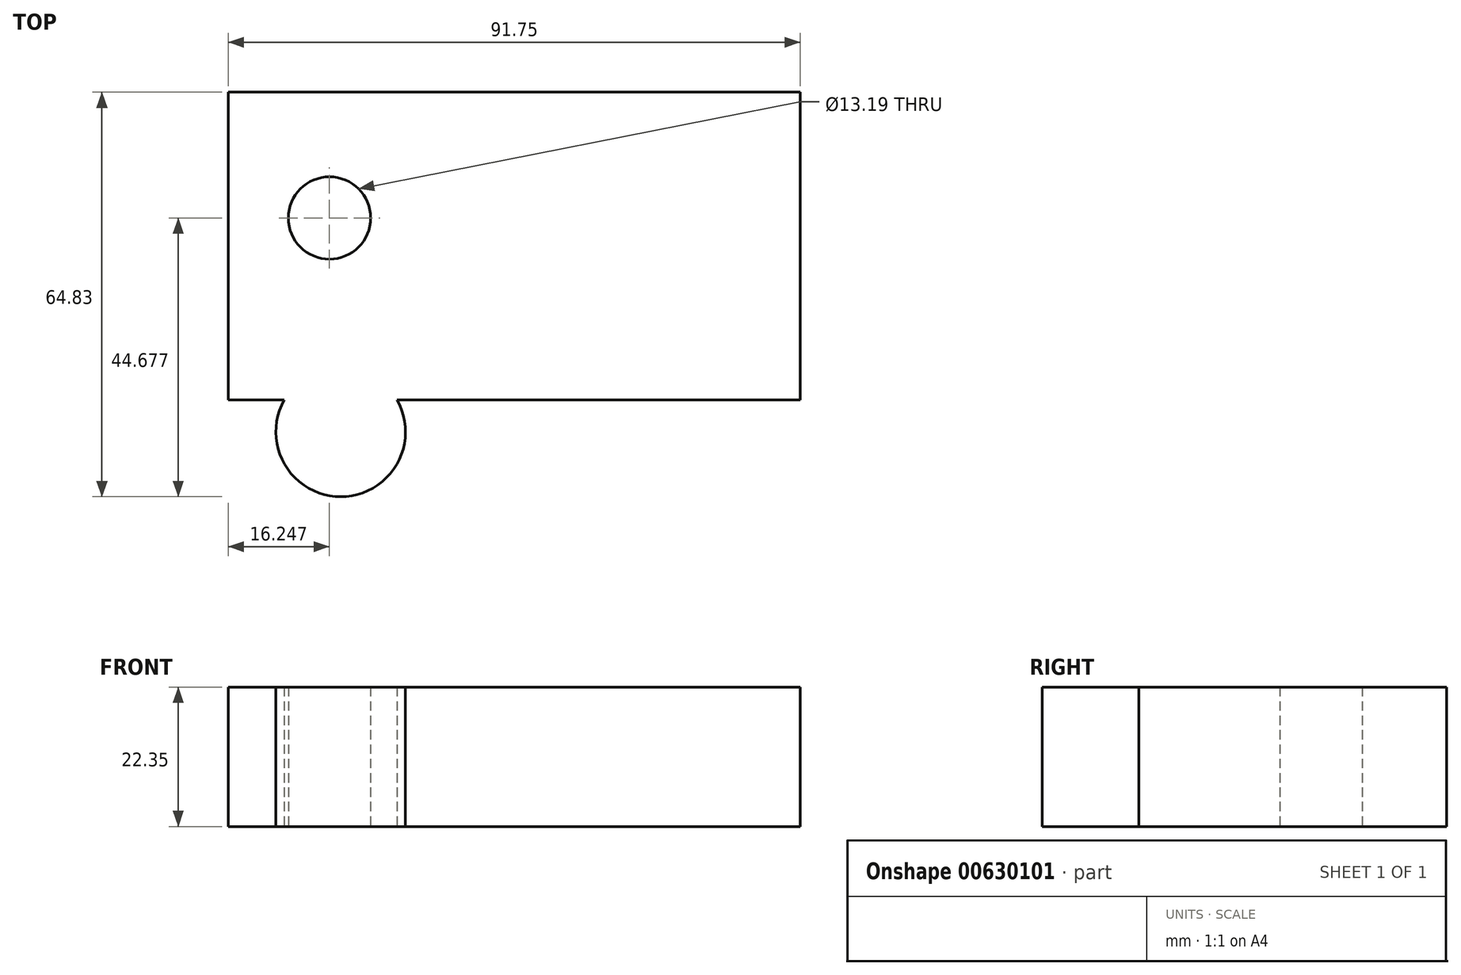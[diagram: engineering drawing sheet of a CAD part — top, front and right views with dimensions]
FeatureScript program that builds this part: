
annotation { "Feature Type Name" : "Feature", "Feature Type Description" : "" }
export const myFeature = defineFeature(function(context is Context, id is Id, definition is map)
    precondition{}
    {
        {
            var Q0;
            Q0=qCreatedBy(makeId("Top.planeOp"),FACE);
            var sketch = newSketch(context, id + "F0", { "sketchPlane" : qUnion([Q0])});
            skLineSegment(sketch, "E0.bottom", {"start": v(-44.07, 30.53) * mm, "end": v(47.68, 30.53) * mm});
            skLineSegment(sketch, "E0.top", {"start": v(-44.07, -18.8) * mm, "end": v(47.68, -18.8) * mm});
            skLineSegment(sketch, "E0.left", {"start": v(-44.07, 30.53) * mm, "end": v(-44.07, -18.8) * mm});
            skLineSegment(sketch, "E0.right", {"start": v(47.68, 30.53) * mm, "end": v(47.68, -18.8) * mm});
            skCircle(sketch, "E1", {"center": v(-27.82, 10.38) * mm, "radius": 6.6 * mm});
            skCircle(sketch, "E2", {"center": v(-26.02, -23.91) * mm, "radius": 10.38 * mm});
            skSolve(sketch);
        }
        {
            var Q0;
            Q0 = qSketchRegion(id + "F0", true);
            extrude(context, id + "F1", {"entities" : qUnion([Q0]), "depth" : 22.35 * mm, "offsetDistance" : 25.4 * mm});
        }
    });
